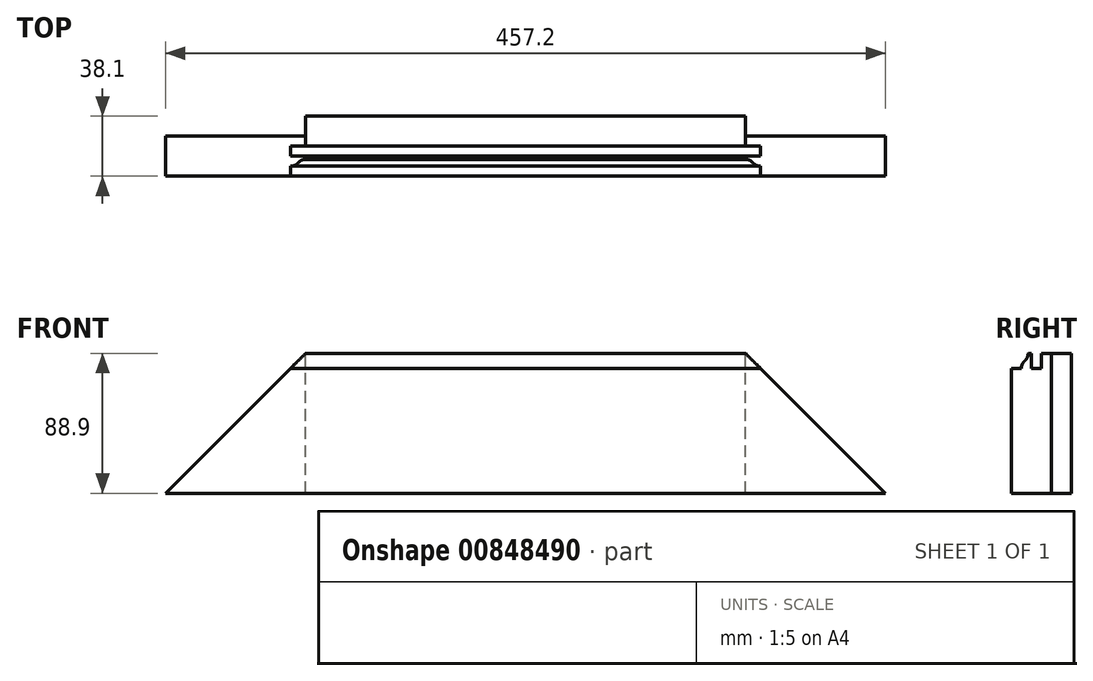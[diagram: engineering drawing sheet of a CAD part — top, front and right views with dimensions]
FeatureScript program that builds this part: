
annotation { "Feature Type Name" : "Feature", "Feature Type Description" : "" }
export const myFeature = defineFeature(function(context is Context, id is Id, definition is map)
    precondition{}
    {
        {
            var Q0;
            Q0=qCreatedBy(makeId("Front.planeOp"),FACE);
            var sketch = newSketch(context, id + "F0", { "sketchPlane" : qUnion([Q0])});
            skLineSegment(sketch, "E0.bottom", {"start": v(-228.6, 44.45) * mm, "end": v(228.6, 44.45) * mm});
            skLineSegment(sketch, "E0.top", {"start": v(-228.6, -44.45) * mm, "end": v(228.6, -44.45) * mm});
            skLineSegment(sketch, "E0.left", {"start": v(-228.6, 44.45) * mm, "end": v(-228.6, -44.45) * mm});
            skLineSegment(sketch, "E0.right", {"start": v(228.6, 44.45) * mm, "end": v(228.6, -44.45) * mm});
            skPoint(sketch, "E0.middle", {"position": v(0, 0) * mm});
            skSolve(sketch);
        }
        {
            var Q0;
            Q0=qSketchRegion(id+"F0",true);
            extrude(context, id + "F1", {"entities" : qUnion([Q0]), "oppositeDirection" : true, "depth" : 38.1 * mm, "offsetDistance" : 25.4 * mm});
        }
        {
            var Q0;
            Q0=makeQuery(id+"F1.opExtrude","SWEPT_FACE",FACE,{"disambiguationData":[OSD([sQuery(id+"F0.wireOp",EDGE,"E0.right")])]});
            var sketch = newSketch(context, id + "F2", { "sketchPlane" : qUnion([Q0])});
            skLineSegment(sketch, "E1", {"start": v(22.22, -38.1) * mm, "end": v(19.05, -44.45) * mm});
            skLineSegment(sketch, "E2", {"start": v(31.75, -44.45) * mm, "end": v(28.57, -38.1) * mm});
            skLineSegment(sketch, "E3", {"start": v(22.22, -38.1) * mm, "end": v(28.57, -38.1) * mm});
            skLineSegment(sketch, "E4", {"start": v(31.75, -44.45) * mm, "end": v(19.05, -44.45) * mm});
            skSolve(sketch);
        }
        {
            var Q0;
            Q0=makeQuery(id+"F1.opExtrude","SWEPT_FACE",FACE,{"disambiguationData":[OSD([sQuery(id+"F0.wireOp",EDGE,"E0.right")])]});
            var sketch = newSketch(context, id + "F3", { "sketchPlane" : qUnion([Q0])});
            skLineSegment(sketch, "E5", {"start": v(0, 34.93) * mm, "end": v(6.35, 34.93) * mm});
            skLineSegment(sketch, "E6", {"start": v(12.7, 34.93) * mm, "end": v(19.05, 34.93) * mm});
            skArc(sketch, "E7", {"start": v(8.5, 39.69) * mm, "mid": v(6.91, 37.54) * mm, "end": v(6.35, 34.93) * mm});
            skLineSegment(sketch, "E8", {"start": v(12.7, 44.45) * mm, "end": v(12.7, 34.93) * mm});
            skLineSegment(sketch, "E9", {"start": v(19.05, 34.93) * mm, "end": v(19.05, 44.45) * mm});
            skLineSegment(sketch, "E10", {"start": v(10.65, 44.45) * mm, "end": v(0, 44.45) * mm});
            skLineSegment(sketch, "E11", {"start": v(0, 44.45) * mm, "end": v(0, 34.93) * mm});
            skLineSegment(sketch, "E12", {"start": v(12.7, 44.45) * mm, "end": v(19.05, 44.45) * mm});
            skArc(sketch, "E13", {"start": v(8.5, 39.69) * mm, "mid": v(10.09, 41.84) * mm, "end": v(10.65, 44.45) * mm});
            skSolve(sketch);
        }
        {
            var Q0;
            Q0=qSketchRegion(id+"F3",true);
            extrude(context, id + "F4", {"entities" : qUnion([Q0]), "operationType" : NewBodyOperationType.REMOVE, "endBound" : BoundingType.THROUGH_ALL, "oppositeDirection" : true, "depth" : 25.4 * mm, "offsetDistance" : 25.4 * mm});
        }
        {
            var Q0;
            Q0=makeQuery(id+"F1.opExtrude","CAP_FACE",FACE,{"disambiguationData":[OSD([sQuery(id+"F0.wireOp",EDGE,"E0.bottom"),sQuery(id+"F0.wireOp",EDGE,"E0.top"),sQuery(id+"F0.wireOp",EDGE,"E0.left"),sQuery(id+"F0.wireOp",EDGE,"E0.right")])],"isStart":true});
            var sketch = newSketch(context, id + "F5", { "sketchPlane" : qUnion([Q0])});
            skLineSegment(sketch, "E14", {"start": v(-228.6, -44.45) * mm, "end": v(-139.7, 44.45) * mm});
            skLineSegment(sketch, "E15", {"start": v(-139.7, 44.45) * mm, "end": v(-228.6, 44.45) * mm});
            skLineSegment(sketch, "E16", {"start": v(-228.6, 44.45) * mm, "end": v(-228.6, -44.45) * mm});
            skPoint(sketch, "E17", {"position": v(-228.6, -4.76) * mm});
            skLineSegment(sketch, "E18", {"start": v(0, 760.27) * mm, "end": v(0, -577.9) * mm, "construction": true});
            skLineSegment(sketch, "E19.MirrorCS", {"start": v(228.6, 44.45) * mm, "end": v(228.6, -44.45) * mm});
            skLineSegment(sketch, "E20.MirrorCS", {"start": v(228.6, -44.45) * mm, "end": v(139.7, 44.45) * mm});
            skLineSegment(sketch, "E21.MirrorCS", {"start": v(139.7, 44.45) * mm, "end": v(228.6, 44.45) * mm});
            skSolve(sketch);
        }
        {
            var Q0;
            Q0=qSketchRegion(id+"F5",true);
            extrude(context, id + "F6", {"entities" : qUnion([Q0]), "operationType" : NewBodyOperationType.REMOVE, "oppositeDirection" : true, "depth" : 25.4 * mm, "offsetDistance" : 25.4 * mm});
        }
        {
            var Q0;
            {var subQ2=sQuery(id+"F0.wireOp",EDGE,"E0.bottom");Q0=makeQuery(id+"F4.boolean.opBoolean","SPLIT",FACE,{"disambiguationData":[TD([makeQuery(id+"F4.opExtrude","SWEPT_FACE",FACE,{"disambiguationData":[OSD([sQuery(id+"F3.wireOp",EDGE,"E9")])]})])],"derivedFrom":makeQuery(id+"F1.opExtrude","SWEPT_FACE",FACE,{"disambiguationData":[OSD([subQ2])]})});}
            var sketch = newSketch(context, id + "F7", { "sketchPlane" : qUnion([Q0])});
            skLineSegment(sketch, "E22.bottom", {"start": v(-228.6, 38.1) * mm, "end": v(-139.7, 38.1) * mm});
            skLineSegment(sketch, "E22.top", {"start": v(-228.6, 25.4) * mm, "end": v(-139.7, 25.4) * mm});
            skLineSegment(sketch, "E22.left", {"start": v(-228.6, 38.1) * mm, "end": v(-228.6, 25.4) * mm});
            skLineSegment(sketch, "E22.right", {"start": v(-139.7, 38.1) * mm, "end": v(-139.7, 25.4) * mm});
            skLineSegment(sketch, "E23", {"start": v(0, 107.05) * mm, "end": v(0, -115.05) * mm, "construction": true});
            skLineSegment(sketch, "E24.MirrorCS", {"start": v(228.6, 38.1) * mm, "end": v(139.7, 38.1) * mm});
            skLineSegment(sketch, "E25.MirrorCS", {"start": v(228.6, 38.1) * mm, "end": v(228.6, 25.4) * mm});
            skLineSegment(sketch, "E26.MirrorCS", {"start": v(228.6, 25.4) * mm, "end": v(139.7, 25.4) * mm});
            skLineSegment(sketch, "E27.MirrorCS", {"start": v(139.7, 38.1) * mm, "end": v(139.7, 25.4) * mm});
            skSolve(sketch);
        }
        {
            var Q0;
            Q0 = qSketchRegion(id + "F7", true);
            extrude(context, id + "F8", {"entities" : qUnion([Q0]), "operationType" : NewBodyOperationType.REMOVE, "endBound" : BoundingType.UP_TO_NEXT, "oppositeDirection" : true, "depth" : 25.4 * mm, "offsetDistance" : 25.4 * mm});
        }
    });
